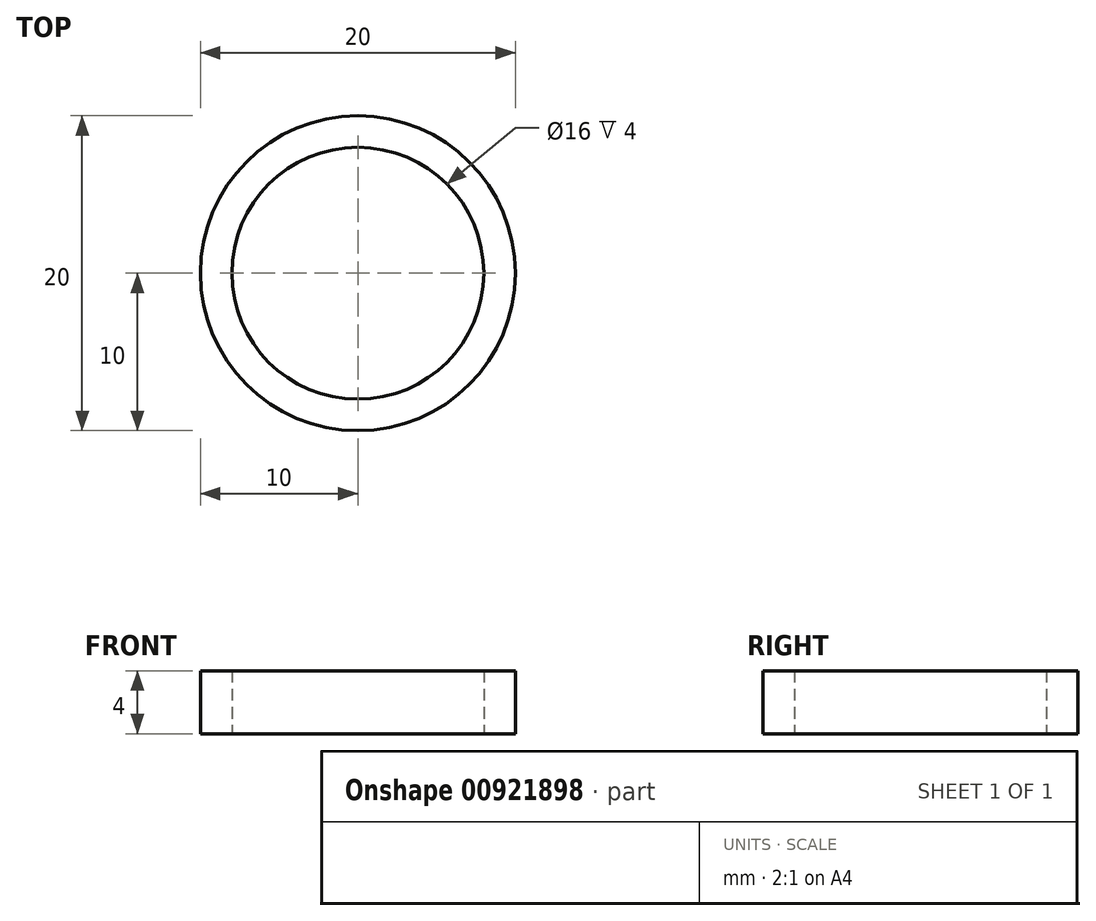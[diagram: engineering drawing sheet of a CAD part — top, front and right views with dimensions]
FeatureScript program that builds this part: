
annotation { "Feature Type Name" : "Feature", "Feature Type Description" : "" }
export const myFeature = defineFeature(function(context is Context, id is Id, definition is map)
    precondition{}
    {
        {
            var Q0;
            Q0=qCreatedBy(makeId("Top.planeOp"),FACE);
            var sketch = newSketch(context, id + "F0", { "sketchPlane" : qUnion([Q0])});
            skCircle(sketch, "E0", {"center": v(0, 0) * mm, "radius": 8 * mm});
            skCircle(sketch, "E1", {"center": v(0, 0) * mm, "radius": 10 * mm});
            skSolve(sketch);
        }
        {
            var Q0;
            Q0=makeQuery(id+"F0.imprint","IMPRINT",FACE,{"disambiguationData":[TD([[makeQuery(id+"F0.imprint","IMPRINT",EDGE,{"derivedFrom":sQuery(id+"F0.wireOp",EDGE,"E0")}),-1.0]])]});
            extrude(context, id + "F1", {"entities" : qUnion([Q0]), "depth" : 4 * mm, "offsetDistance" : 25 * mm});
        }
    });
